# Revit family: Touch Panel _ST7-X
name_source: partatom
category: Generic Models
revit_build: Autodesk Revit 2018 (Build: 20170223_1515(x64)
units: mm (PartAtom-declared; Revit-internal decimal feet)

## family parameters
Always vertical = Yes
Can host rebar = No
Cut with Voids When Loaded = No
Part Type = Normal
Room Calculation Point = No
Round Connector Dimension = Use Diameter
Shared = No
Work Plane-Based = Yes

## types (1)
- ST7-B/W
    Ambient temperature = 0°C to +40°C
    Bluetooth = V2.1 + EDR/BT v3.0/BT v3.0 +HS/BT v4.0
    Brightness = 350 cd/m²
    Default Elevation = 0 mm  [stored 0 ft]
    Dimension = 181.5mm x121.5mm x25.8mm
    Environment = Complies with WEEE and RoHS directives
    IP Code = IP40 (user access)
    Input Voltage = 9 VDC - 24 VDC
    LAN = 1 x RJ45 10/100 Mb/s,Cat 5E upto 100m. For router network.
    Manufacturer = Helvar
    Model = ST7-X
    Mounting = In-wall(solid and plasterboard walls)
    RED = EN 300 328
EN 301 489-1
EN 301 489-17
    Relative humidity = Max. 90%, noncondensing
    Resolution = 1024 x 600
    Safety = EN 60950-1
    Screen = 7" IPS
    Storage temperature = -20°C to +70°C
    Typical power consumption = 6 W
    Weight = 350 g

note: [stored X ft] marks values corroborated as IEEE doubles in the binary element streams (Revit-internal decimal feet)

## geometry (parser evidence)
native form markers: Sweep x2
no freeform markers — native parametric forms only
